# Revit family: R586R_131-143
name_source: partatom
category: Pipe Accessories
units: mm (PartAtom-declared; Revit-internal decimal feet)

## family parameters
Always vertical = No
Cut with Voids When Loaded = No
Part Type = Normal
Round Connector Dimension = Use Diameter
Shared = No
Work Plane-Based = No

## types (4) — shared parameters
C = 125 mm  [stored 0.410105 ft]
D = 250 mm  [stored 0.82021 ft]
F = 430 mm  [stored 1.41076 ft]
G = 100 mm  [stored 0.328084 ft]
GIA_Description = Distribution groups and regulation
GIA_Manufacturer = GIACOMINI
GIA_Model = R586R
H = 65 mm  [stored 0.213255 ft]
I = 165 mm
L = 160 mm  [stored 0.524934 ft]
Manufacturer = Giacomini
Nominal Diameter 1 = 40 mm  [stored 0.131234 ft]
Nominal Diameter 2 = 25 mm  [stored 0.082021 ft]
zero-valued in all types: Default Elevation

## per-type parameters (varying)
| type | GIA_Code | Void Position |
| R586RY131-with circulator | R586RY131 | 145 mm  [stored 0.475722 ft] |
| R586RY133-with circulator | R586RY133 | 145 mm  [stored 0.475722 ft] |
| R586RY141-without circulator | R586RY141 | 300 mm |
| R586RY143-without circulator | R586RY143 | 300 mm |

note: column(s) folded — value = type name in every type: Model

note: [stored X ft] marks values corroborated as IEEE doubles in the binary element streams (Revit-internal decimal feet)

## geometry (parser evidence)
native form markers: Sweep x11
no freeform markers — native parametric forms only
